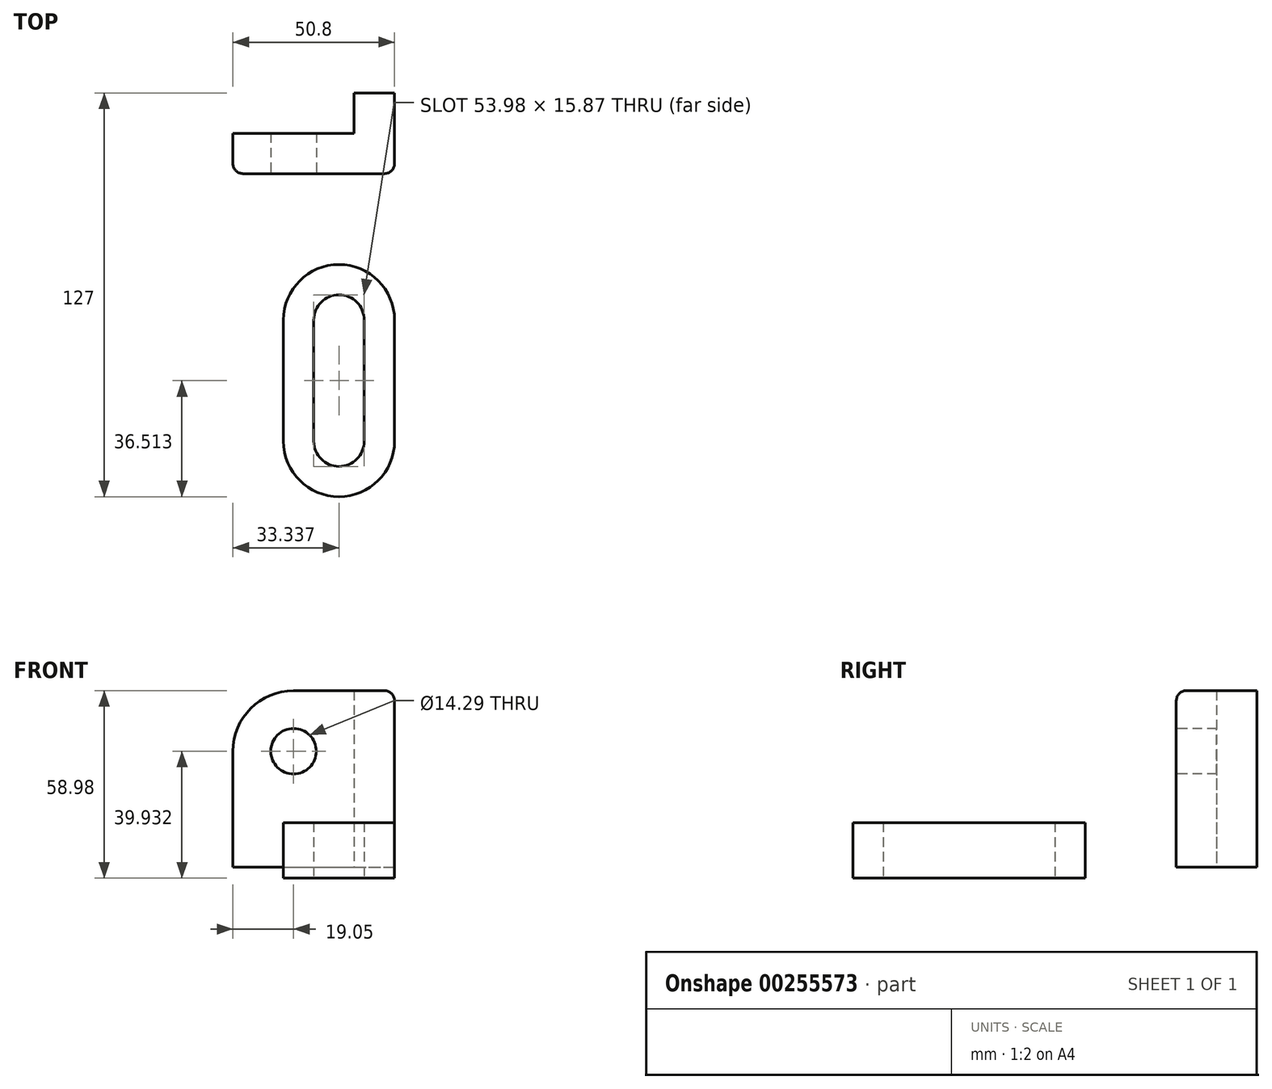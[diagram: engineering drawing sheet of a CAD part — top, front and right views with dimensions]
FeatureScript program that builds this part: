
annotation { "Feature Type Name" : "Feature", "Feature Type Description" : "" }
export const myFeature = defineFeature(function(context is Context, id is Id, definition is map)
    precondition{}
    {
        {
            var Q0;
            Q0=qCreatedBy(makeId("Front.planeOp"),FACE);
            var sketch = newSketch(context, id + "F0", { "sketchPlane" : qUnion([Q0])});
            skLineSegment(sketch, "E0.bottom", {"start": v(-31.75, 58.98) * mm, "end": v(0, 58.98) * mm});
            skLineSegment(sketch, "E0.top", {"start": v(-50.8, 3.42) * mm, "end": v(0, 3.42) * mm});
            skLineSegment(sketch, "E0.left", {"start": v(-50.8, 39.93) * mm, "end": v(-50.8, 3.42) * mm});
            skLineSegment(sketch, "E0.right", {"start": v(0, 58.98) * mm, "end": v(0, 3.42) * mm});
            skPoint(sketch, "E1.visualSharp", {"position": v(-50.8, 58.98) * mm});
            skArc(sketch, "E1.filletArc", {"start": v(-31.75, 58.98) * mm, "mid": v(-45.22, 53.4) * mm, "end": v(-50.8, 39.93) * mm});
            skSolve(sketch);
        }
        {
            var Q0;
            Q0=makeQuery(id+"F0.imprint","IMPRINT",FACE,{"disambiguationData":[TD([[makeQuery(id+"F0.imprint","IMPRINT",EDGE,{"derivedFrom":sQuery(id+"F0.wireOp",EDGE,"E0.bottom")}),-1.0]])]});
            extrude(context, id + "F1", {"entities" : qUnion([Q0]), "depth" : 12.7 * mm});
        }
        {
            var Q0;
            Q0=makeQuery(id+"F1.opExtrude","CAP_FACE",FACE,{"disambiguationData":[OSD([sQuery(id+"F0.wireOp",EDGE,"E0.bottom"),sQuery(id+"F0.wireOp",EDGE,"E0.top"),sQuery(id+"F0.wireOp",EDGE,"E0.left"),sQuery(id+"F0.wireOp",EDGE,"E0.right"),sQuery(id+"F0.wireOp",EDGE,"E1.filletArc")])],"isStart":true});
            var sketch = newSketch(context, id + "F2", { "sketchPlane" : qUnion([Q0])});
            skLineSegment(sketch, "E2.bottom", {"start": v(0, 58.98) * mm, "end": v(12.7, 58.98) * mm});
            skLineSegment(sketch, "E2.top", {"start": v(0, 3.42) * mm, "end": v(12.7, 3.42) * mm});
            skLineSegment(sketch, "E2.left", {"start": v(0, 58.98) * mm, "end": v(0, 3.42) * mm});
            skLineSegment(sketch, "E2.right", {"start": v(12.7, 58.98) * mm, "end": v(12.7, 3.42) * mm});
            skSolve(sketch);
        }
        {
            var Q0;
            Q0 = qSketchRegion(id + "F2", true);
            extrude(context, id + "F3", {"entities" : qUnion([Q0]), "operationType" : NewBodyOperationType.ADD, "depth" : 12.7 * mm});
        }
        {
            var Q0;
            Q0=qCreatedBy(makeId("Top.planeOp"),FACE);
            var sketch = newSketch(context, id + "F4", { "sketchPlane" : qUnion([Q0])});
            skLineSegment(sketch, "E3", {"start": v(-55.63, 0) * mm, "end": v(-55.63, -96.84) * mm, "construction": true});
            skLineSegment(sketch, "E4", {"start": v(-55.63, -96.84) * mm, "end": v(-17.46, -96.84) * mm, "construction": true});
            skLineSegment(sketch, "E5", {"start": v(78.97, -96.84) * mm, "end": v(78.97, -58.74) * mm, "construction": true});
            skLineSegment(sketch, "E6", {"start": v(78.97, -58.74) * mm, "end": v(-34.92, -58.74) * mm, "construction": true});
            skLineSegment(sketch, "E7", {"start": v(-17.46, 11.68) * mm, "end": v(-17.46, -66.67) * mm, "construction": true});
            skPoint(sketch, "E8.orphan", {"position": v(-17.46, 0) * mm});
            skCircle(sketch, "E9", {"center": v(-17.46, -96.84) * mm, "radius": 7.94 * mm});
            skCircle(sketch, "E10", {"center": v(-17.46, -58.74) * mm, "radius": 7.94 * mm});
            skArc(sketch, "E11.0", {"start": v(0, -58.74) * mm, "mid": v(-17.46, -41.27) * mm, "end": v(-34.92, -58.74) * mm});
            skLineSegment(sketch, "E12", {"start": v(0, 0.58) * mm, "end": v(0, -96.84) * mm});
            skPoint(sketch, "E13.orphan", {"position": v(0, -39.77) * mm});
            skLineSegment(sketch, "E14", {"start": v(-34.92, -58.74) * mm, "end": v(-34.92, -96.84) * mm});
            skLineSegment(sketch, "E15", {"start": v(-9.52, -58.74) * mm, "end": v(-9.52, -96.84) * mm});
            skLineSegment(sketch, "E16", {"start": v(-25.4, -58.74) * mm, "end": v(-25.4, -96.84) * mm});
            skArc(sketch, "E17.trimOffspring", {"start": v(-34.92, -96.84) * mm, "mid": v(-17.46, -114.3) * mm, "end": v(0, -96.84) * mm});
            skLineSegment(sketch, "E18.trimOffspring", {"start": v(-17.46, -88.9) * mm, "end": v(-17.46, -96.84) * mm, "construction": true});
            skLineSegment(sketch, "E19.trimOffspring", {"start": v(-9.52, -96.84) * mm, "end": v(91.53, -96.84) * mm, "construction": true});
            skSolve(sketch);
        }
        {
            var Q0;
            Q0=makeQuery(id+"F1.opExtrude","CAP_FACE",FACE,{"disambiguationData":[OSD([sQuery(id+"F0.wireOp",EDGE,"E0.bottom"),sQuery(id+"F0.wireOp",EDGE,"E0.top"),sQuery(id+"F0.wireOp",EDGE,"E0.left"),sQuery(id+"F0.wireOp",EDGE,"E0.right"),sQuery(id+"F0.wireOp",EDGE,"E1.filletArc")])],"isStart":false});
            var sketch = newSketch(context, id + "F5", { "sketchPlane" : qUnion([Q0])});
            skLineSegment(sketch, "E20.0", {"start": v(-31.75, 39.93) * mm, "end": v(-31.75, 39.93) * mm});
            skCircle(sketch, "E21", {"center": v(-31.75, 39.93) * mm, "radius": 7.14 * mm});
            skSolve(sketch);
        }
        {
            var Q0;
            Q0=makeQuery(id+"F5.imprint","IMPRINT",FACE,{"disambiguationData":[TD([[makeQuery(id+"F5.imprint","IMPRINT",EDGE,{"derivedFrom":sQuery(id+"F5.wireOp",EDGE,"E21")}),1.0]])]});
            extrude(context, id + "F6", {"entities" : qUnion([Q0]), "operationType" : NewBodyOperationType.REMOVE, "oppositeDirection" : true, "depth" : 12.7 * mm});
        }
        {
            var Q0;
            Q0=makeQuery(id+"F1.opExtrude","CAP_EDGE",EDGE,{"disambiguationData":[OSD([sQuery(id+"F0.wireOp",EDGE,"E1.filletArc")])],"isStart":false});
            fillet(context, id + "F7", {"entities" : qUnion([Q0]), "radius" : 3.17 * mm, "tangentPropagation" : true, "allowEdgeOverflow" : false});
        }
        {
            var Q0;
            Q0=makeQuery(id+"F1.opExtrude","CAP_EDGE",EDGE,{"disambiguationData":[OSD([sQuery(id+"F0.wireOp",EDGE,"E0.right")])],"isStart":false});
            fillet(context, id + "F8", {"entities" : qUnion([Q0]), "radius" : 3.17 * mm, "tangentPropagation" : true, "allowEdgeOverflow" : false});
        }
        {
            var Q0;
            Q0 = qSketchRegion(id + "F4", true);
            extrude(context, id + "F9", {"entities" : qUnion([Q0]), "depth" : 17.46 * mm});
        }
    });
